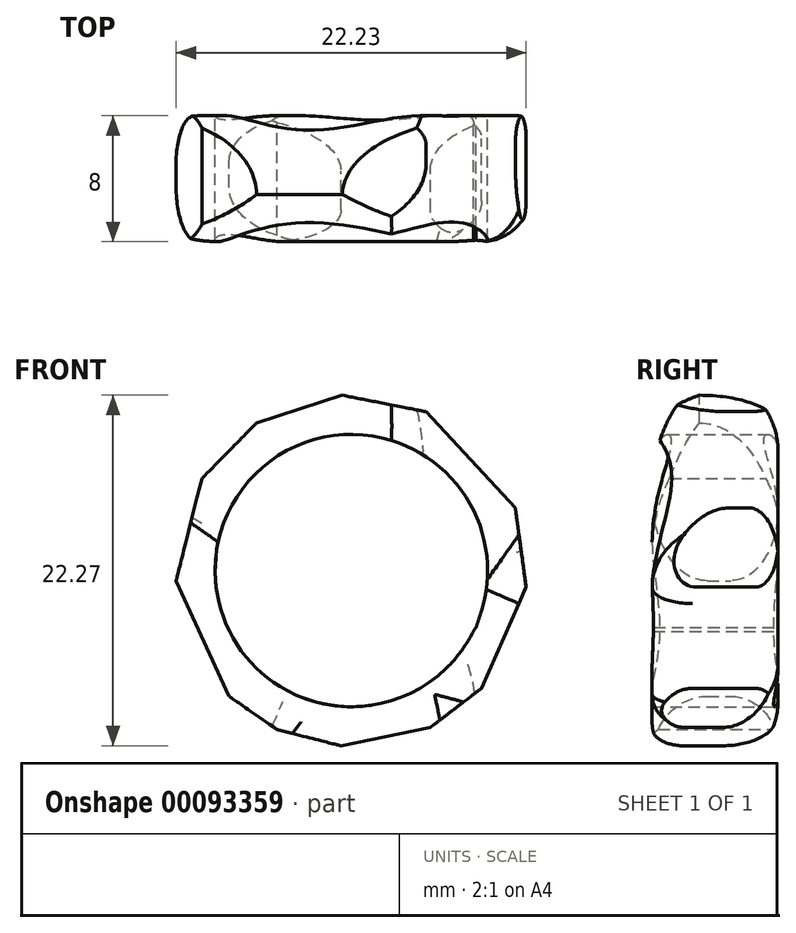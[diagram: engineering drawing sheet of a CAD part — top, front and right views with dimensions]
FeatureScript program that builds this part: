
annotation { "Feature Type Name" : "Feature", "Feature Type Description" : "" }
export const myFeature = defineFeature(function(context is Context, id is Id, definition is map)
    precondition{}
    {
        {
            var Q0;
            Q0=qCreatedBy(makeId("Front.planeOp"),FACE);
            var sketch = newSketch(context, id + "F0", { "sketchPlane" : qUnion([Q0])});
            skCircle(sketch, "E0", {"center": v(0, 0) * mm, "radius": 8.65 * mm});
            skCircle(sketch, "E1.0", {"center": v(0, 0) * mm, "radius": 11.15 * mm});
            skLineSegment(sketch, "E2", {"start": v(4.75, 10.09) * mm, "end": v(10.41, 3.99) * mm});
            skLineSegment(sketch, "E3", {"start": v(10.41, 3.99) * mm, "end": v(11.1, -1.06) * mm});
            skLineSegment(sketch, "E4", {"start": v(11.1, -1.06) * mm, "end": v(8.27, -7.48) * mm});
            skLineSegment(sketch, "E5", {"start": v(8.27, -7.48) * mm, "end": v(5, -9.96) * mm});
            skLineSegment(sketch, "E6", {"start": v(5, -9.96) * mm, "end": v(-0.66, -11.13) * mm});
            skLineSegment(sketch, "E7", {"start": v(-0.66, -11.13) * mm, "end": v(-4.73, -10.1) * mm});
            skLineSegment(sketch, "E8", {"start": v(-4.73, -10.1) * mm, "end": v(-7.78, -7.99) * mm});
            skLineSegment(sketch, "E9", {"start": v(-7.78, -7.99) * mm, "end": v(-11.13, -0.65) * mm});
            skLineSegment(sketch, "E10", {"start": v(-11.13, -0.65) * mm, "end": v(-9.5, 5.84) * mm});
            skLineSegment(sketch, "E11", {"start": v(-9.5, 5.84) * mm, "end": v(-6.02, 9.38) * mm});
            skLineSegment(sketch, "E12", {"start": v(-6.02, 9.38) * mm, "end": v(-0.56, 11.14) * mm});
            skLineSegment(sketch, "E13", {"start": v(-0.56, 11.14) * mm, "end": v(4.75, 10.09) * mm});
            skLineSegment(sketch, "E14", {"start": v(4.75, 10.09) * mm, "end": v(6.22, 6.02) * mm});
            skLineSegment(sketch, "E15", {"start": v(6.22, 6.02) * mm, "end": v(10.41, 3.99) * mm});
            skLineSegment(sketch, "E16", {"start": v(10.41, 3.99) * mm, "end": v(7.92, -3.6) * mm});
            skLineSegment(sketch, "E17", {"start": v(7.92, -3.6) * mm, "end": v(3.26, -10.32) * mm});
            skLineSegment(sketch, "E18", {"start": v(3.26, -10.32) * mm, "end": v(-3.38, -7.96) * mm});
            skLineSegment(sketch, "E19", {"start": v(-3.38, -7.96) * mm, "end": v(-8.79, -5.79) * mm});
            skLineSegment(sketch, "E20", {"start": v(-8.79, -5.79) * mm, "end": v(-8.56, -1.27) * mm});
            skLineSegment(sketch, "E21", {"start": v(-8.56, -1.27) * mm, "end": v(-10.15, 3.24) * mm});
            skLineSegment(sketch, "E22", {"start": v(-10.15, 3.24) * mm, "end": v(-4, 7.66) * mm});
            skLineSegment(sketch, "E23", {"start": v(-4, 7.66) * mm, "end": v(-1.86, 10.72) * mm});
            skLineSegment(sketch, "E24", {"start": v(-1.86, 10.72) * mm, "end": v(2.32, 8.33) * mm});
            skSolve(sketch);
        }
        {
            var Q0;
            {var subQ0=sQuery(id+"F0.wireOp",EDGE,"E15");Q0=makeQuery(id+"F0.imprint","IMPRINT",FACE,{"disambiguationData":[TD([[makeQuery(id+"F0.imprint","IMPRINT",EDGE,{"derivedFrom":subQ0}),-1.0]])]});}
            var Q1;
            {var subQ0=sQuery(id+"F0.wireOp",EDGE,"E13");Q1=makeQuery(id+"F0.imprint","IMPRINT",FACE,{"disambiguationData":[TD([[makeQuery(id+"F0.imprint","IMPRINT",EDGE,{"derivedFrom":subQ0}),-1.0]])]});}
            var Q2;
            {var subQ0=sQuery(id+"F0.wireOp",EDGE,"E23");Q2=makeQuery(id+"F0.imprint","IMPRINT",FACE,{"disambiguationData":[TD([[makeQuery(id+"F0.imprint","IMPRINT",EDGE,{"derivedFrom":subQ0}),-1.0]])]});}
            var Q3;
            {var subQ1=sQuery(id+"F0.wireOp",EDGE,"E11");Q3=makeQuery(id+"F0.imprint","IMPRINT",FACE,{"disambiguationData":[TD([[makeQuery(id+"F0.imprint","IMPRINT",EDGE,{"derivedFrom":subQ1}),-1.0]])]});}
            var Q4;
            {var subQ0=sQuery(id+"F0.wireOp",EDGE,"E21");Q4=makeQuery(id+"F0.imprint","IMPRINT",FACE,{"disambiguationData":[TD([[makeQuery(id+"F0.imprint","IMPRINT",EDGE,{"derivedFrom":subQ0}),-1.0]])]});}
            var Q5;
            {var subQ3=sQuery(id+"F0.wireOp",EDGE,"E20");Q5=makeQuery(id+"F0.imprint","IMPRINT",FACE,{"disambiguationData":[TD([[makeQuery(id+"F0.imprint","IMPRINT",EDGE,{"derivedFrom":subQ3}),1.0]])]});}
            var Q6;
            {var subQ0=sQuery(id+"F0.wireOp",EDGE,"E19");Q6=makeQuery(id+"F0.imprint","IMPRINT",FACE,{"disambiguationData":[TD([[makeQuery(id+"F0.imprint","IMPRINT",EDGE,{"derivedFrom":subQ0}),-1.0]])]});}
            var Q7;
            {var subQ2=sQuery(id+"F0.wireOp",EDGE,"E7");Q7=makeQuery(id+"F0.imprint","IMPRINT",FACE,{"disambiguationData":[TD([[makeQuery(id+"F0.imprint","IMPRINT",EDGE,{"derivedFrom":subQ2}),-1.0]])]});}
            var Q8;
            {var subQ0=sQuery(id+"F0.wireOp",EDGE,"E18");var subQ1=sQuery(id+"F0.wireOp",EDGE,"E0");var subQ2=makeQuery(id+"F0.imprint","INTERSECT",VERTEX,{"derivedFrom":[subQ1,subQ0]});Q8=makeQuery(id+"F0.imprint","IMPRINT",FACE,{"disambiguationData":[TD([[makeQuery(id+"F0.imprint","IMPRINT",EDGE,{"disambiguationData":[TD([[subQ2,-1.0]])],"derivedFrom":subQ1}),-1.0]])]});}
            var Q9;
            {var subQ7=sQuery(id+"F0.wireOp",EDGE,"E3");Q9=makeQuery(id+"F0.imprint","IMPRINT",FACE,{"disambiguationData":[TD([[makeQuery(id+"F0.imprint","IMPRINT",EDGE,{"derivedFrom":subQ7}),-1.0]])]});}
            var Q10;
            Q10=makeQuery(id+"F0.imprint","IMPRINT",FACE,{"disambiguationData":[TD([[makeQuery(id+"F0.imprint","IMPRINT",EDGE,{"derivedFrom":sQuery(id+"F0.wireOp",EDGE,"E2")}),-1.0]])]});
            extrude(context, id + "F1", {"entities" : qUnion([Q0, Q1, Q2, Q3, Q4, Q5, Q6, Q7, Q8, Q9, Q10]), "flatOperationType" : FlatOperationType.REMOVE, "depth" : 4 * mm, "hasSecondDirection" : true, "secondDirectionOppositeDirection" : true, "secondDirectionDepth" : 4 * mm, "offsetDistance" : 25 * mm, "domain" : OperationDomain.MODEL});
        }
        {
            var Q0;
            Q0=makeQuery(id+"F1.opExtrude","CAP_EDGE",EDGE,{"disambiguationData":[OSD([sQuery(id+"F0.wireOp",EDGE,"E2")])],"isStart":false});
            fillet(context, id + "F2", {"entities" : qUnion([Q0]), "radius" : 5 * mm, "tangentPropagation" : true, "allowEdgeOverflow" : false});
        }
        {
            var Q0;
            Q0=makeQuery(id+"F1.opExtrude","CAP_EDGE",EDGE,{"disambiguationData":[OSD([sQuery(id+"F0.wireOp",EDGE,"E4")])],"isStart":true});
            fillet(context, id + "F3", {"entities" : qUnion([Q0]), "radius" : 1.45 * mm, "tangentPropagation" : true, "allowEdgeOverflow" : false});
        }
        {
            var Q0;
            Q0=makeQuery(id+"F1.opExtrude","CAP_EDGE",EDGE,{"disambiguationData":[OSD([sQuery(id+"F0.wireOp",EDGE,"E4")])],"isStart":false});
            fillet(context, id + "F4", {"entities" : qUnion([Q0]), "radius" : 2.58 * mm, "tangentPropagation" : true, "allowEdgeOverflow" : false});
        }
        {
            var Q0;
            Q0=makeQuery(id+"F1.opExtrude","CAP_EDGE",EDGE,{"disambiguationData":[OSD([sQuery(id+"F0.wireOp",EDGE,"E2")])],"isStart":true});
            fillet(context, id + "F5", {"entities" : qUnion([Q0]), "radius" : 1.89 * mm, "tangentPropagation" : true, "allowEdgeOverflow" : false});
        }
        {
            var Q0;
            Q0=makeQuery(id+"F1.opExtrude","CAP_EDGE",EDGE,{"disambiguationData":[OSD([sQuery(id+"F0.wireOp",EDGE,"E12")])],"isStart":true});
            fillet(context, id + "F6", {"entities" : qUnion([Q0]), "radius" : 5 * mm, "tangentPropagation" : true, "allowEdgeOverflow" : false});
        }
        {
            var Q0;
            Q0=makeQuery(id+"F1.opExtrude","CAP_EDGE",EDGE,{"disambiguationData":[OSD([sQuery(id+"F0.wireOp",EDGE,"E12")])],"isStart":false});
            fillet(context, id + "F7", {"entities" : qUnion([Q0]), "radius" : 8.63 * mm, "tangentPropagation" : true, "allowEdgeOverflow" : false});
        }
        {
            var Q0;
            Q0=makeQuery(id+"F1.opExtrude","CAP_EDGE",EDGE,{"disambiguationData":[OSD([sQuery(id+"F0.wireOp",EDGE,"E9")])],"isStart":false});
            var Q1;
            Q1=makeQuery(id+"F1.opExtrude","CAP_EDGE",EDGE,{"disambiguationData":[OSD([sQuery(id+"F0.wireOp",EDGE,"E6")])],"isStart":true});
            fillet(context, id + "F8", {"entities" : qUnion([Q0, Q1]), "radius" : 3.5 * mm, "tangentPropagation" : true, "allowEdgeOverflow" : false});
        }
        {
            var Q0;
            Q0=makeQuery(id+"F1.opExtrude","CAP_EDGE",EDGE,{"disambiguationData":[OSD([sQuery(id+"F0.wireOp",EDGE,"E9")])],"isStart":true});
            fillet(context, id + "F9", {"entities" : qUnion([Q0]), "radius" : 3 * mm, "tangentPropagation" : true, "allowEdgeOverflow" : false});
        }
        {
            var Q0;
            Q0=makeQuery(id+"F1.opExtrude","CAP_EDGE",EDGE,{"disambiguationData":[OSD([sQuery(id+"F0.wireOp",EDGE,"E6")])],"isStart":false});
            fillet(context, id + "F10", {"entities" : qUnion([Q0]), "radius" : 2 * mm, "tangentPropagation" : true, "allowEdgeOverflow" : false});
        }
    });
